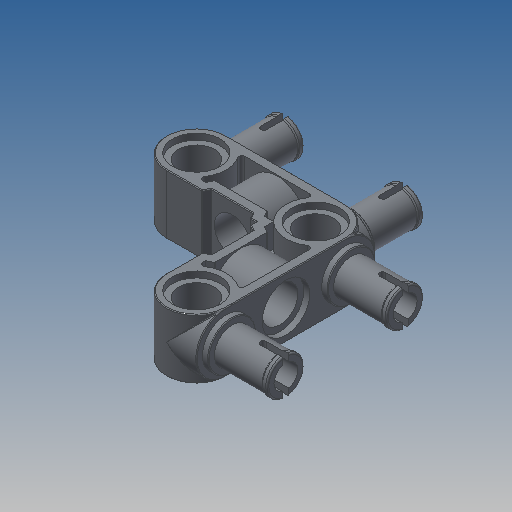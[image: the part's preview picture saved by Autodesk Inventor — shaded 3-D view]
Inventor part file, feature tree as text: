
AUTODESK INVENTOR PART (.ipt)
format: ipt  version: 2022.2 (Build 262287000, 287)  size: 1,093,120 bytes
history: native  units: in
note: dims shown in document units (in); Inventor stores cm internally (conversion verified against a paired STEP export)
features: extrude x8, sketch x4, mirror x2, revolve x1, pattern_linear x1, plane x1, fillet x1
ambient origin geometry x8: Origin, YZ Plane, XZ Plane, XY Plane, X Axis, Y Axis, Z Axis, Center Point
bodies: Solid1 (feature_tree)
feature tree (18):
  sketch  "Sketch2"  dims[d0=0.315in d1=0.189in]
  extrude  "Extrusion1"  Depth=0.189in
  extrude  "Extrusion2"  Depth=0.6299in
  sketch  "Sketch3"  dims[d2=0.252in d3=0.6299in]
  extrude  "Extrusion3"  Depth=0.0315in
  extrude  "Extrusion4"  Depth=0.0079in
  extrude  "Extrusion5"  Depth=0.0079in
  extrude  "Extrusion6"  Depth=0.0079in
  sketch  "Sketch4"  dims[d4=45.0deg d5=0.0315in]
  revolve  "Revolution1"  [1 undecoded]
  extrude  "Extrusion7"  TaperAngle=0.0deg  [1 undecoded]
  pattern_linear  "Rectangular Pattern1"  Spacing1=0.063in  [1 undecoded]
  extrude  "Extrusion8"  TaperAngle=0.0deg  [1 undecoded]
  mirror  "Mirror1"
  plane  "Work Plane1"
  mirror  "Mirror2"
  fillet  "Fillet1"  Radius=0.063in
  sketch  "Sketch5"  dims[d6=0.0315in d7=0.801in d8=0.801in d9=0.2205in d10=0.315in d11=0.0in d12=0.063in d13=0.0in d14=0.063in d15=0.0in d16=0.252in d17=0.189in d18=0.3071in d19=0.063in d20=0.0in d21=0.063in d22=0.0in d23=0.0315in d24=0.0in d25=0.252in d26=0.189in d27=0.126in d28=0.1969in d29=0.0315in d30=0.315in d31=0.0315in d32=0.1339in d33=90.0deg d34=0.0315in d35=0.0in d36=0.7874in d38=0.6299in d39=0.252in d40=0.0315in d41=0.0in d42=0.0039in d43=0.0in d44=0.0in d45=0.0in d46=0.0in d47=0.0157in d50=0.0079in]
note: 4 required parameter values undecoded (feature->parameter linkage not recoverable at this tier; creation-order binding heuristic only, values carry confidence <= 0.55)